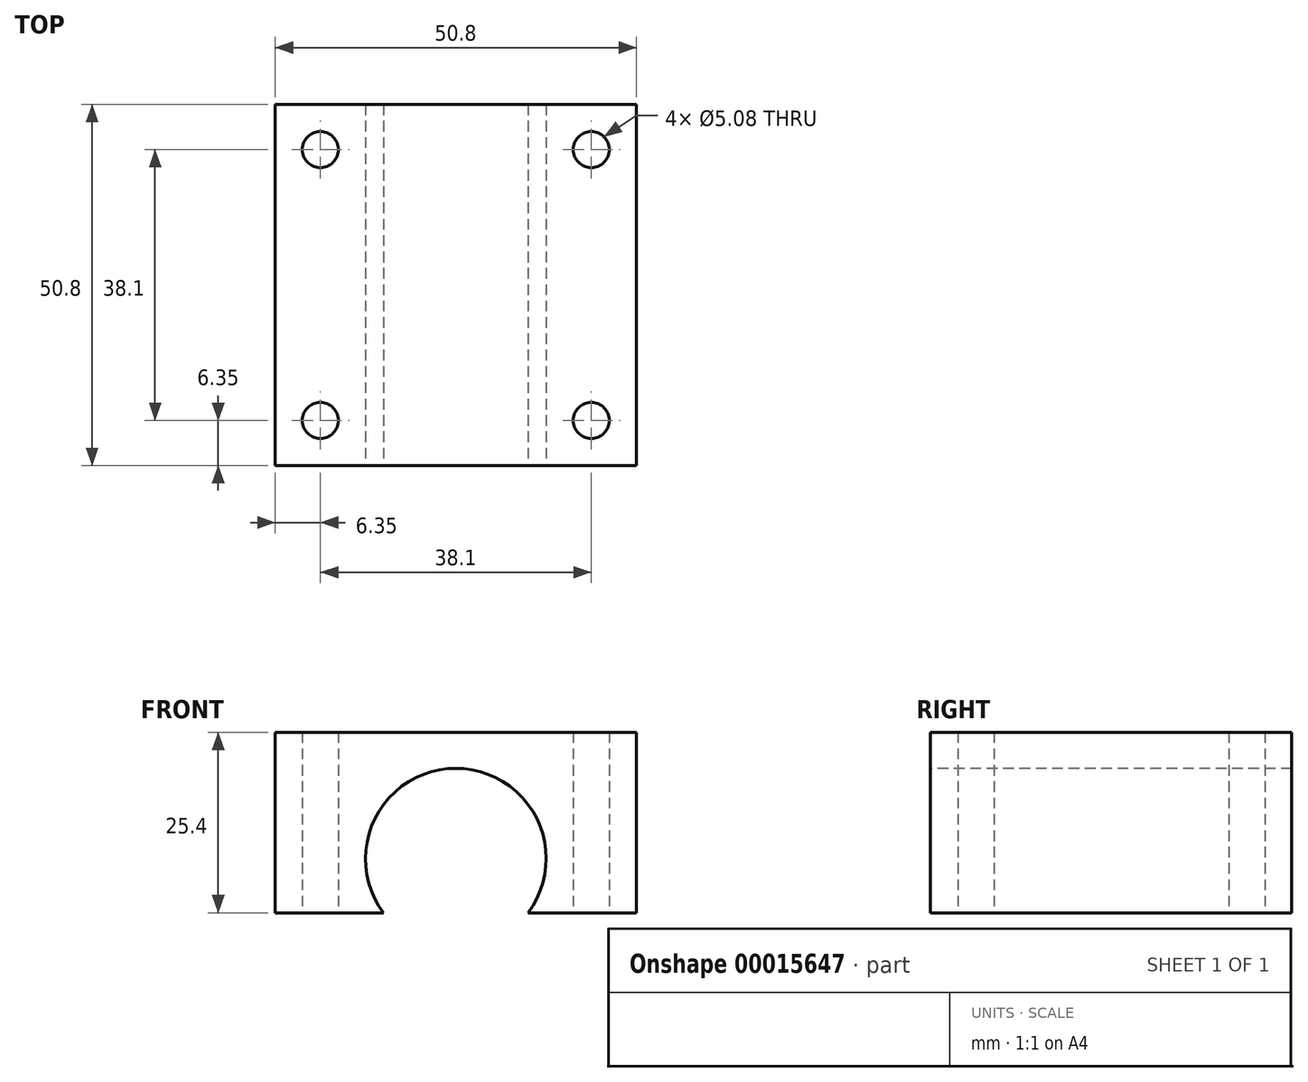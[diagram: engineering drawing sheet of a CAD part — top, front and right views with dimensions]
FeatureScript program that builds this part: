
annotation { "Feature Type Name" : "Feature", "Feature Type Description" : "" }
export const myFeature = defineFeature(function(context is Context, id is Id, definition is map)
    precondition{}
    {
        {
            var Q0;
            Q0=qCreatedBy(makeId("Top.planeOp"),FACE);
            var sketch = newSketch(context, id + "F0", { "sketchPlane" : qUnion([Q0])});
            skLineSegment(sketch, "E0.bottom", {"start": v(0, 0) * mm, "end": v(50.8, 0) * mm});
            skLineSegment(sketch, "E0.top", {"start": v(0, 50.8) * mm, "end": v(50.8, 50.8) * mm});
            skLineSegment(sketch, "E0.left", {"start": v(0, 0) * mm, "end": v(0, 50.8) * mm});
            skLineSegment(sketch, "E0.right", {"start": v(50.8, 0) * mm, "end": v(50.8, 50.8) * mm});
            skCircle(sketch, "E1", {"center": v(6.35, 44.45) * mm, "radius": 2.54 * mm});
            skLineSegment(sketch, "E2", {"start": v(25.4, 50.8) * mm, "end": v(25.4, 0) * mm, "construction": true});
            skLineSegment(sketch, "E3", {"start": v(0, 25.4) * mm, "end": v(50.8, 25.4) * mm, "construction": true});
            skCircle(sketch, "E4.MirrorC", {"center": v(44.45, 44.45) * mm, "radius": 2.54 * mm});
            skCircle(sketch, "E5.MirrorC", {"center": v(6.35, 6.35) * mm, "radius": 2.54 * mm});
            skCircle(sketch, "E6.MirrorC", {"center": v(44.45, 6.35) * mm, "radius": 2.54 * mm});
            skSolve(sketch);
        }
        {
            var Q0;
            Q0=makeQuery(id+"F0.imprint","IMPRINT",FACE,{"disambiguationData":[TD([[makeQuery(id+"F0.imprint","IMPRINT",EDGE,{"derivedFrom":sQuery(id+"F0.wireOp",EDGE,"E0.bottom")}),1.0]])]});
            extrude(context, id + "F1", {"entities" : qUnion([Q0]), "depth" : 25.4 * mm});
        }
        {
            var Q0;
            Q0=makeQuery(id+"F1.opExtrude","SWEPT_FACE",FACE,{"disambiguationData":[OSD([sQuery(id+"F0.wireOp",EDGE,"E0.bottom")])]});
            var sketch = newSketch(context, id + "F2", { "sketchPlane" : qUnion([Q0])});
            skArc(sketch, "E7", {"start": v(35.56, 0) * mm, "mid": v(25.4, 20.32) * mm, "end": v(15.24, 0) * mm});
            skLineSegment(sketch, "E8", {"start": v(25.4, 0) * mm, "end": v(25.4, 25.4) * mm, "construction": true});
            skSolve(sketch);
        }
        {
            var Q0;
            {var subQ1=sQuery(id+"F2.wireOp",EDGE,"E7");Q0=makeQuery(id+"F2.imprint","IMPRINT",FACE,{"disambiguationData":[TD([[makeQuery(id+"F2.imprint","IMPRINT",EDGE,{"derivedFrom":subQ1}),1.0]])]});}
            extrude(context, id + "F3", {"entities" : qUnion([Q0]), "operationType" : NewBodyOperationType.REMOVE, "endBound" : BoundingType.UP_TO_NEXT, "oppositeDirection" : true, "depth" : 25.4 * mm});
        }
    });
